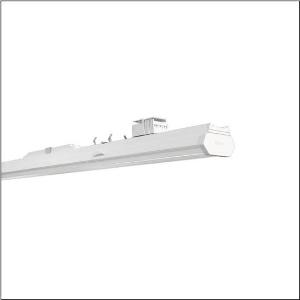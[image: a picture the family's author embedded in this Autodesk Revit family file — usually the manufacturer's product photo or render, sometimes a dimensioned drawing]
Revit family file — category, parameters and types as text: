
# Revit family: licross_r__11_protected_mo_51ts12dn58xf_38fb
name_source: partatom
category: Lighting Fixtures
units: mm (PartAtom-declared; Revit-internal decimal feet)

## family parameters
Cut with Voids When Loaded = No
Host = Face
Light Source = No
Part Type = Normal
Room Calculation Point = No
Round Connector Dimension = Use Diameter
Shared = No

## types (1)
- --- (1 x LED, 8480 lm, 56.2 W, 5000K)
    Apparent Load = 56 VA
    CIE Flux Codes = 54 82 95 97 100
    Color Rendering = 80
    Color Temperature = 5000K
    Default Elevation = 1800 mm
    Description = Licross® 11 Protected MO, luminaire insert, of sheet steel, galvanised, coil coated, white, length: 1.500mm, width: 90mm, height: 101mm, LED rated luminous flux: 8.480lm, light colour: 850, control gear: DALI 2, control gear: ECG DALI, with plug, 5-pole, with phase selection, mains connection: 220..240V, AC, 50/60Hz, rated input power: 56W, halogen-free wiring, primary optical cover: cover, of PMMA, light emission: direct distribution, primary light characteristic: symmetric, protection rating (complete): IP50, insulation class (complete): insulation class I (protective earthing), certification: CE, ENEC, VDE, UKCA, protection symbol: D if used in an environment with non-conductive dust loads with corresponding accessories, impact resistance: IK06, permissible ambient temperature for indoor applications: -25..+40°C, reducing of maximum allowable ambient temperature of 5°C with ceiling mounting, corresponds to IFS (International Featured Standards) requirements for safety and quality in the food industry, LABS conformity tested according to VDMA 24364:2018-05, packaging unit: 1 piece
    Height = 92 mm
    Lamp = 1 x LED
    Lamp Light Flux = 8480 lm
    Lamp Power = 56.2 W
    Lamp count = 1
    Length = 1500 mm
    Luminous efficacy = 151 lm/W
    Manufacturer = Siteco
    ModVariant = No
    Model = 51TS12DN58XF
    Mounting Place = Ceiling
    Mounting Type = Pendant
    Number of Poles = 1
    OnlyDefault = Yes
    Power Factor = 1
    Product Name = Licross® 11 Protected MO
    Product group = luminaire insert
    ProductGroupID = 901
    Protection Class = Protection class I
    Protection Degree = IP 50
    RLX_Detail_Level = 1
    RLX_Emergency_Light_Flux = 0 lm
    RLX_Emergency_Type = 0
    RLX_Emergency_Type_DB = No
    RlxData = <blob elided: 24025 chars, md5=e529fb3c>
    Socket = socket
    Standby Power = 0 W
    System Light Flux = 8480 lm
    System Power = 56 W
    Type Comments = factory setting: luminous flux: 100 % | dim-lin: 254 | 370 mA
    Type Image = l_1256145.jpg
    URL = http://relux.com
    VarID = @adj_143753
    Voltage = 0 V
    Weight = 0.00 kg
    Width = 88 mm

## geometry (parser evidence)
native form markers: Blend x4, Sweep x13
no freeform markers — native parametric forms only
